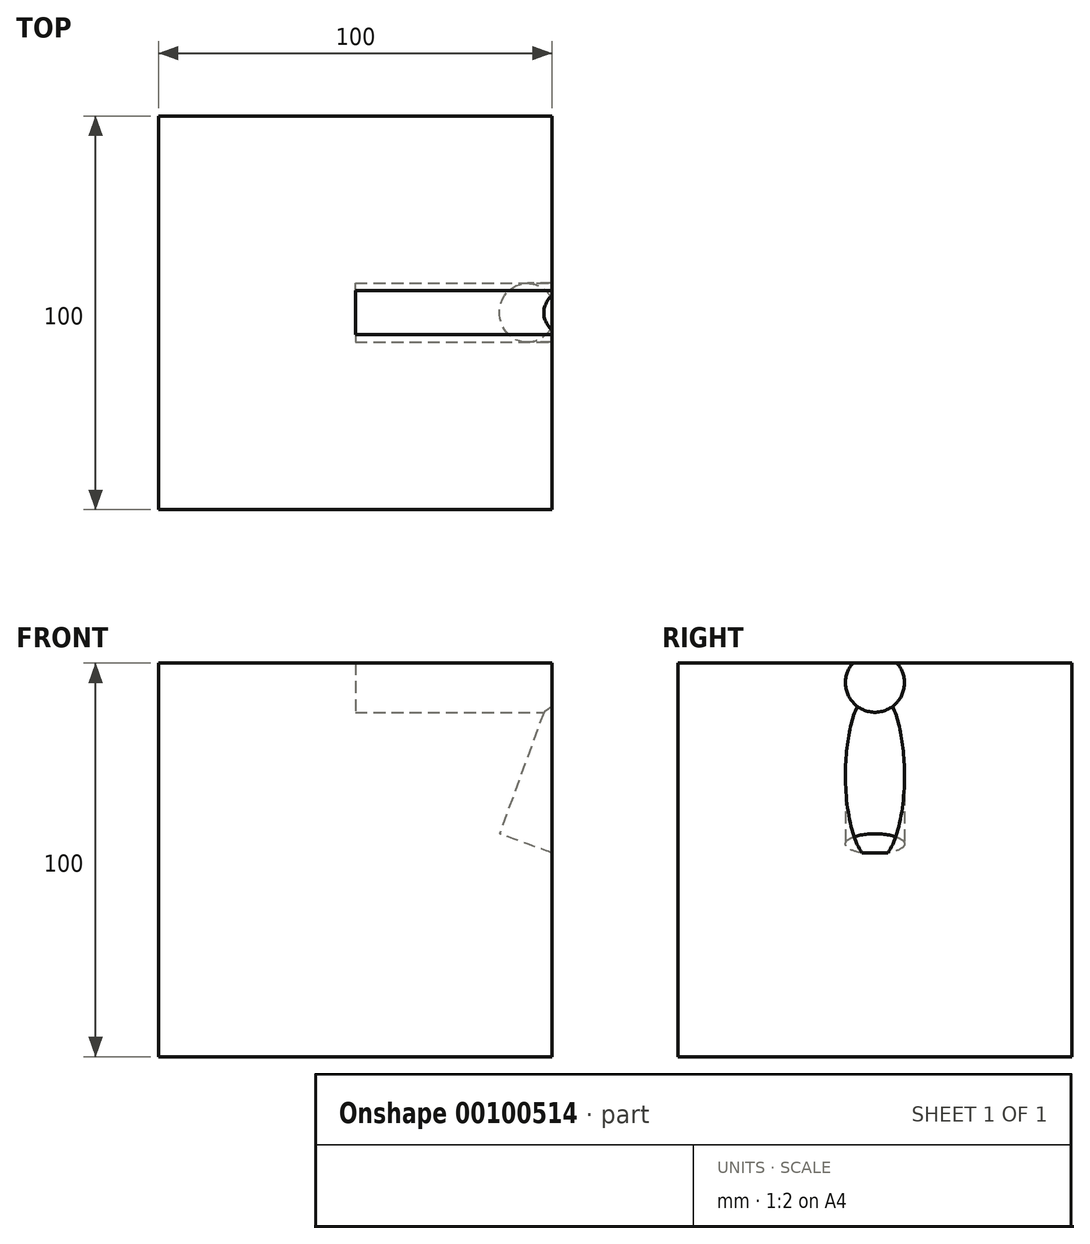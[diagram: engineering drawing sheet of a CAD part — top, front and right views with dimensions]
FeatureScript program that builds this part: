
annotation { "Feature Type Name" : "Feature", "Feature Type Description" : "" }
export const myFeature = defineFeature(function(context is Context, id is Id, definition is map)
    precondition{}
    {
        {
            var Q0;
            Q0=qCreatedBy(makeId("Front.planeOp"),FACE);
            var sketch = newSketch(context, id + "F0", { "sketchPlane" : qUnion([Q0])});
            skLineSegment(sketch, "E0.bottom", {"start": v(50, 50) * mm, "end": v(-50, 50) * mm});
            skLineSegment(sketch, "E0.top", {"start": v(50, -50) * mm, "end": v(-50, -50) * mm});
            skLineSegment(sketch, "E0.left", {"start": v(50, 50) * mm, "end": v(50, -50) * mm});
            skLineSegment(sketch, "E0.right", {"start": v(-50, 50) * mm, "end": v(-50, -50) * mm});
            skPoint(sketch, "E0.middle", {"position": v(0, 0) * mm});
            skSolve(sketch);
        }
        {
            var Q0;
            Q0 = qSketchRegion(id + "F0", true);
            extrude(context, id + "F1", {"entities" : qUnion([Q0]), "depth" : 50 * mm, "hasSecondDirection" : true, "secondDirectionOppositeDirection" : true, "secondDirectionDepth" : 50 * mm});
        }
        {
            var Q0;
            Q0=qCreatedBy(makeId("Front.planeOp"),FACE);
            var sketch = newSketch(context, id + "F2", { "sketchPlane" : qUnion([Q0])});
            skLineSegment(sketch, "E1", {"start": v(0, 0) * mm, "end": v(0, 25) * mm});
            skLineSegment(sketch, "E2", {"start": v(0, 25) * mm, "end": v(30, 25) * mm});
            skLineSegment(sketch, "E3", {"start": v(30, 25) * mm, "end": v(24.87, 10.9) * mm});
            skSolve(sketch);
        }
        {
            var Q0;
            Q0=qCreatedBy(makeId("Right.planeOp"),FACE);
            var sketch = newSketch(context, id + "F3", { "sketchPlane" : qUnion([Q0])});
            skCircle(sketch, "E4", {"center": v(0, 45) * mm, "radius": 7.5 * mm});
            skSolve(sketch);
        }
        {
            var Q0;
            Q0=makeQuery(id+"F3.imprint","IMPRINT",FACE,{"disambiguationData":[TD([[makeQuery(id+"F3.imprint","IMPRINT",EDGE,{"derivedFrom":sQuery(id+"F3.wireOp",EDGE,"E4")}),1.0]])]});
            var Q1;
            Q1=sQuery(id+"F2.wireOp",EDGE,"E2");
            var Q2;
            Q2=sQuery(id+"F2.wireOp",EDGE,"E3");
            sweep(context, id + "F4", {"operationType" : NewBodyOperationType.REMOVE, "profiles" : qUnion([Q0]), "path" : qUnion([Q1, Q2])});
        }
    });
